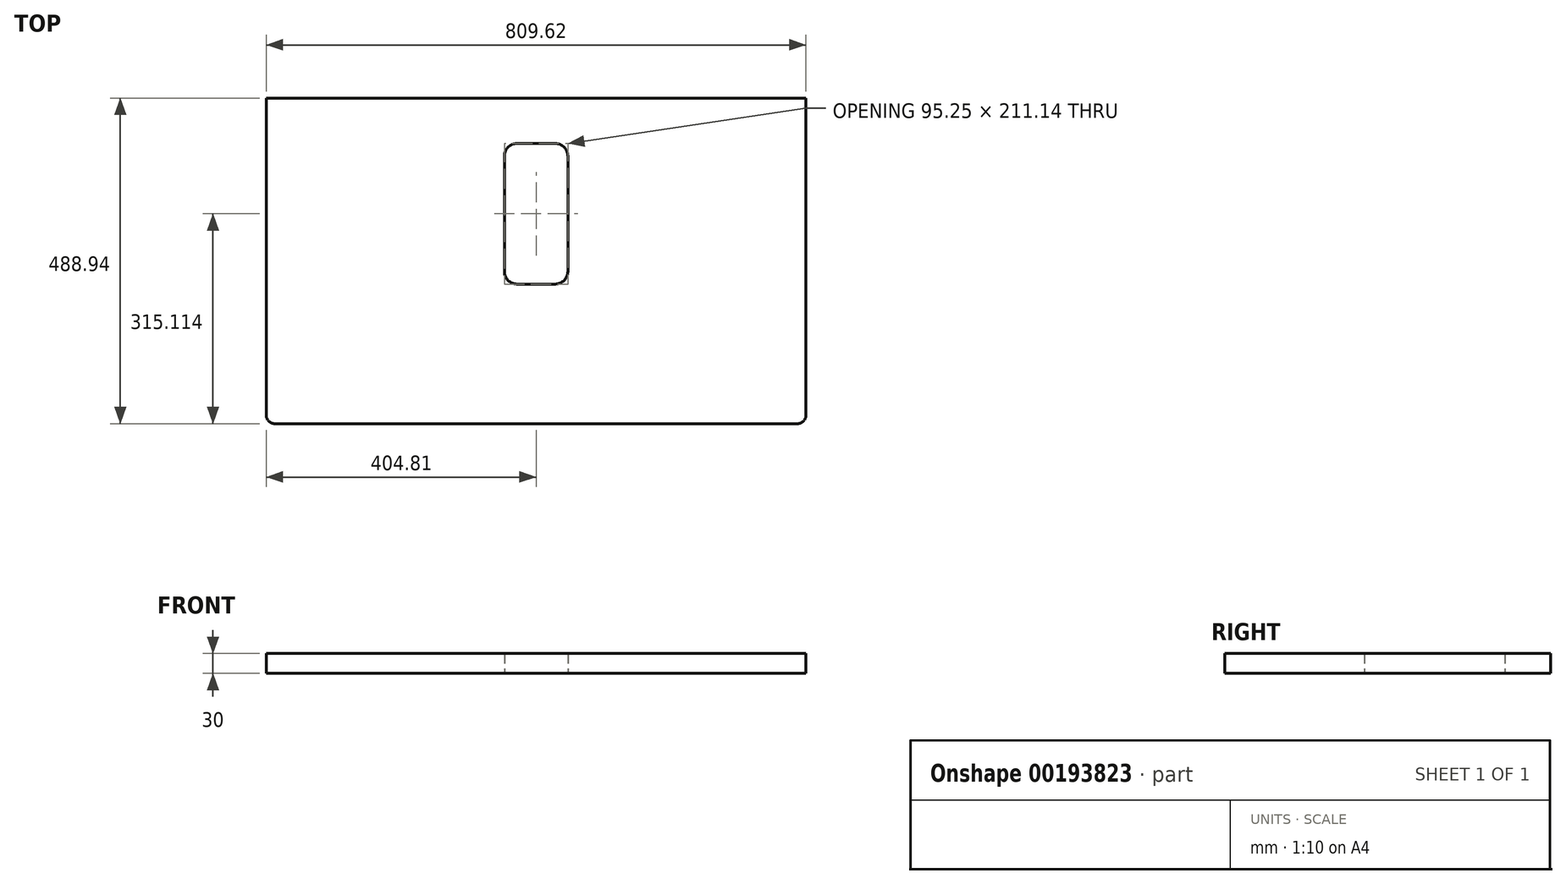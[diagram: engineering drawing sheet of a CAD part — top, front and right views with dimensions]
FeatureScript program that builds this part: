
annotation { "Feature Type Name" : "Feature", "Feature Type Description" : "" }
export const myFeature = defineFeature(function(context is Context, id is Id, definition is map)
    precondition{}
    {
        {
            var Q0;
            Q0=qCreatedBy(makeId("Top.planeOp"),FACE);
            var sketch = newSketch(context, id + "F0", { "sketchPlane" : qUnion([Q0])});
            skLineSegment(sketch, "E0.bottom", {"start": v(-404.81, 244.48) * mm, "end": v(404.81, 244.48) * mm});
            skLineSegment(sketch, "E0.top", {"start": v(-392.11, -244.48) * mm, "end": v(392.11, -244.48) * mm});
            skLineSegment(sketch, "E0.left", {"start": v(-404.81, 244.48) * mm, "end": v(-404.81, -231.78) * mm});
            skLineSegment(sketch, "E0.right", {"start": v(404.81, 244.48) * mm, "end": v(404.81, -231.78) * mm});
            skCircle(sketch, "E1", {"center": v(0, 0) * mm, "radius": 215.9 * mm, "construction": true});
            skCircle(sketch, "E2", {"center": v(0, 11.97) * mm, "radius": 21.5 * mm, "construction": true});
            skLineSegment(sketch, "E3.bottom", {"start": v(-28.58, 176.21) * mm, "end": v(28.57, 176.21) * mm});
            skLineSegment(sketch, "E3.top", {"start": v(-28.58, -34.93) * mm, "end": v(28.58, -34.93) * mm});
            skLineSegment(sketch, "E3.left", {"start": v(-47.63, 157.16) * mm, "end": v(-47.62, -15.88) * mm});
            skLineSegment(sketch, "E3.right", {"start": v(47.62, 157.16) * mm, "end": v(47.63, -15.88) * mm});
            skLineSegment(sketch, "E4", {"start": v(0, 176.21) * mm, "end": v(0, 0) * mm, "construction": true});
            skPoint(sketch, "E5.visualSharp", {"position": v(-47.62, 176.21) * mm});
            skArc(sketch, "E5.filletArc", {"start": v(-28.58, 176.21) * mm, "mid": v(-42.05, 170.63) * mm, "end": v(-47.63, 157.16) * mm});
            skPoint(sketch, "E6.visualSharp", {"position": v(47.62, 176.21) * mm});
            skArc(sketch, "E6.filletArc", {"start": v(47.62, 157.16) * mm, "mid": v(42.05, 170.63) * mm, "end": v(28.57, 176.21) * mm});
            skPoint(sketch, "E7.visualSharp", {"position": v(47.63, -34.93) * mm});
            skArc(sketch, "E7.filletArc", {"start": v(28.58, -34.93) * mm, "mid": v(42.05, -29.35) * mm, "end": v(47.63, -15.88) * mm});
            skPoint(sketch, "E8.visualSharp", {"position": v(-47.62, -34.93) * mm});
            skArc(sketch, "E8.filletArc", {"start": v(-47.62, -15.88) * mm, "mid": v(-42.05, -29.35) * mm, "end": v(-28.58, -34.93) * mm});
            skPoint(sketch, "E9.visualSharp", {"position": v(-404.81, -244.48) * mm});
            skArc(sketch, "E9.filletArc", {"start": v(-404.81, -231.78) * mm, "mid": v(-401.1, -240.76) * mm, "end": v(-392.11, -244.48) * mm});
            skPoint(sketch, "E10.visualSharp", {"position": v(404.81, -244.47) * mm});
            skArc(sketch, "E10.filletArc", {"start": v(392.11, -244.48) * mm, "mid": v(401.1, -240.76) * mm, "end": v(404.81, -231.78) * mm});
            skPoint(sketch, "E11", {"position": v(0, 244.48) * mm});
            skLineSegment(sketch, "E12", {"start": v(404.81, -244.48) * mm, "end": v(-404.81, 244.48) * mm, "construction": true});
            skSolve(sketch);
        }
        {
            var Q0;
            Q0=makeQuery(id+"F0.imprint","IMPRINT",FACE,{"disambiguationData":[TD([[makeQuery(id+"F0.imprint","IMPRINT",EDGE,{"derivedFrom":sQuery(id+"F0.wireOp",EDGE,"E0.bottom")}),-1.0]])]});
            extrude(context, id + "F1", {"entities" : qUnion([Q0]), "depth" : 30 * mm});
        }
    });
